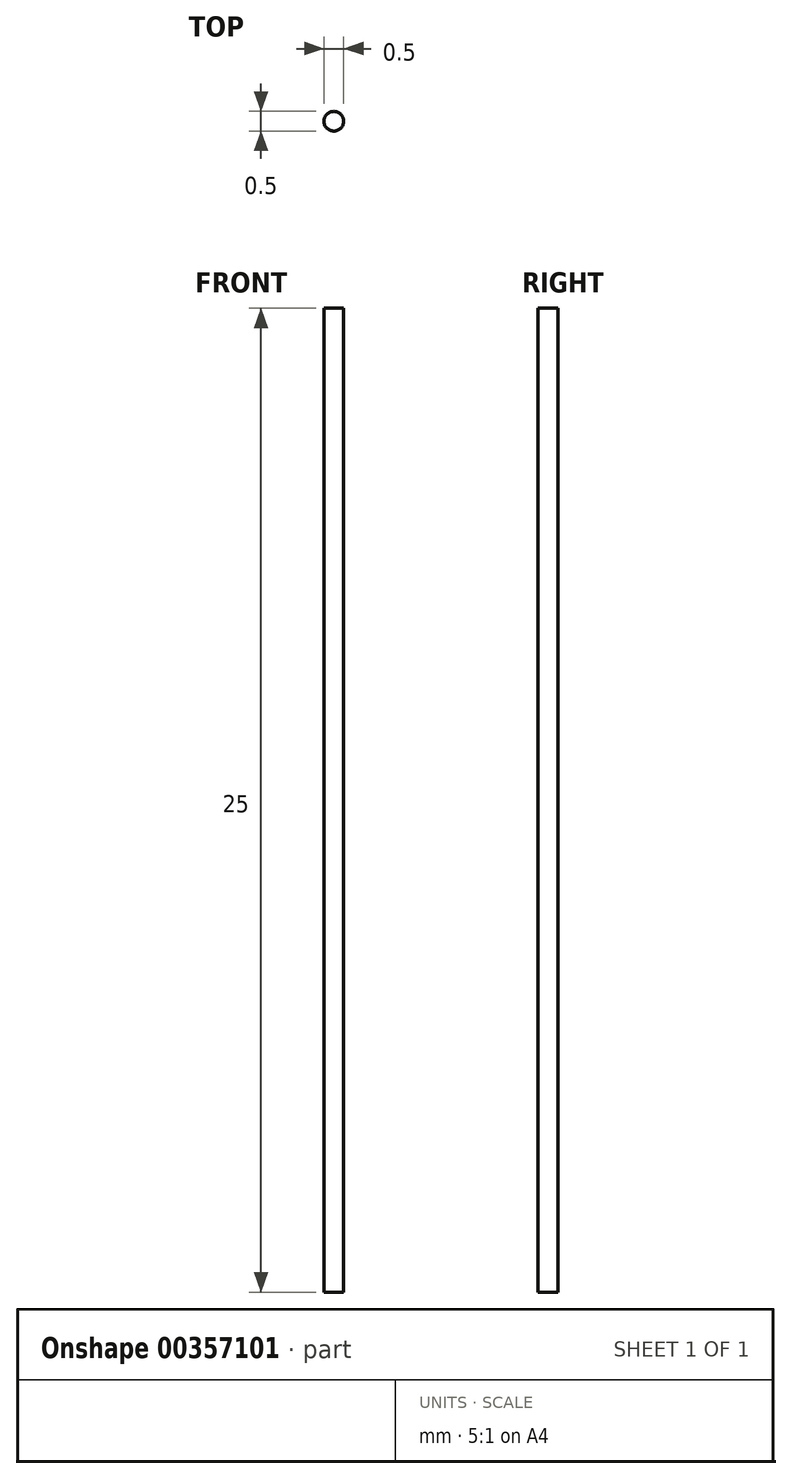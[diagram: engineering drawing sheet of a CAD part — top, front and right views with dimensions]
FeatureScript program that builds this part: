
annotation { "Feature Type Name" : "Feature", "Feature Type Description" : "" }
export const myFeature = defineFeature(function(context is Context, id is Id, definition is map)
    precondition{}
    {
        {
            var Q0;
            Q0=qCreatedBy(makeId("Top.planeOp"),FACE);
            var sketch = newSketch(context, id + "F0", { "sketchPlane" : qUnion([Q0])});
            skCircle(sketch, "E0", {"center": v(0, 0) * mm, "radius": 0.25 * mm});
            skSolve(sketch);
        }
        {
            var Q0;
            Q0 = qSketchRegion(id + "F0", true);
            extrude(context, id + "F1", {"entities" : qUnion([Q0]), "endBound" : BoundingType.SYMMETRIC, "depth" : 25 * mm});
        }
    });
